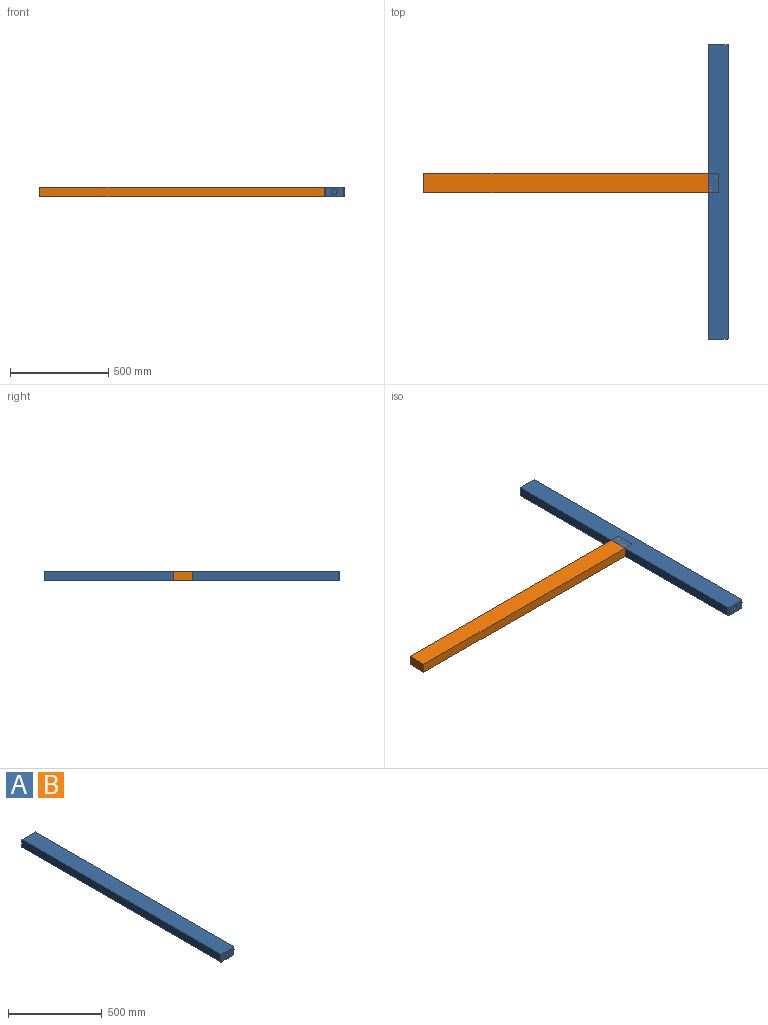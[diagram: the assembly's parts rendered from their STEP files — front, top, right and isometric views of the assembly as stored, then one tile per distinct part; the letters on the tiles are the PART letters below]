
ASSEMBLY  parts=2 mates=1
PART A: 10 faces, bbox 100x1500x55 mm
  f0: plane 1495x50mm, normal (1,0,0), area 74750mm2, adj f1,f3,f5,f7
  f1: plane 1500x100mm, normal (0,0,1), area 149991.7mm2, adj f0,f2,f4,f5,f6,f7
  f2: plane 1495x50mm, normal (-1,0,0), area 74750mm2, adj f1,f3,f5,f6
  f3: plane 1500x100mm, normal (0,0,-1), area 149991.7mm2, adj f0,f2,f4,f5,f6,f7
  f4: plane 90x50mm, normal (0,-1,0), area 3824.1mm2, adj f1,f3,f6,f7,f8
  f5: plane 100x50mm, normal (0,1,0), area 5000mm2, adj f0,f1,f2,f3
  f6: bspline ~55x5mm, area 405.8mm2, adj f1,f2,f3,f4
  f7: bspline ~55x5mm, area 405.8mm2, adj f0,f1,f3,f4
  f8: cylinder r=14.67mm len=29.34mm, axis (0,-1,0), area 2304.1mm2, adj f4,f9
  f9: plane 29.34x29.34mm, normal (0,-1,0), area 675.9mm2, adj f8
PART B: same geometry as A
PLACE A t=(-368.71,419.17,-176.98)mm
PLACE B rot(axis=(0,0,1),90deg) t=(-1868.71,-285.79,-176.98)mm
MATE planar B.f1 <-> A.f1  axis (0,0,1) through (-368.71,-330.79,-151.98)mm
